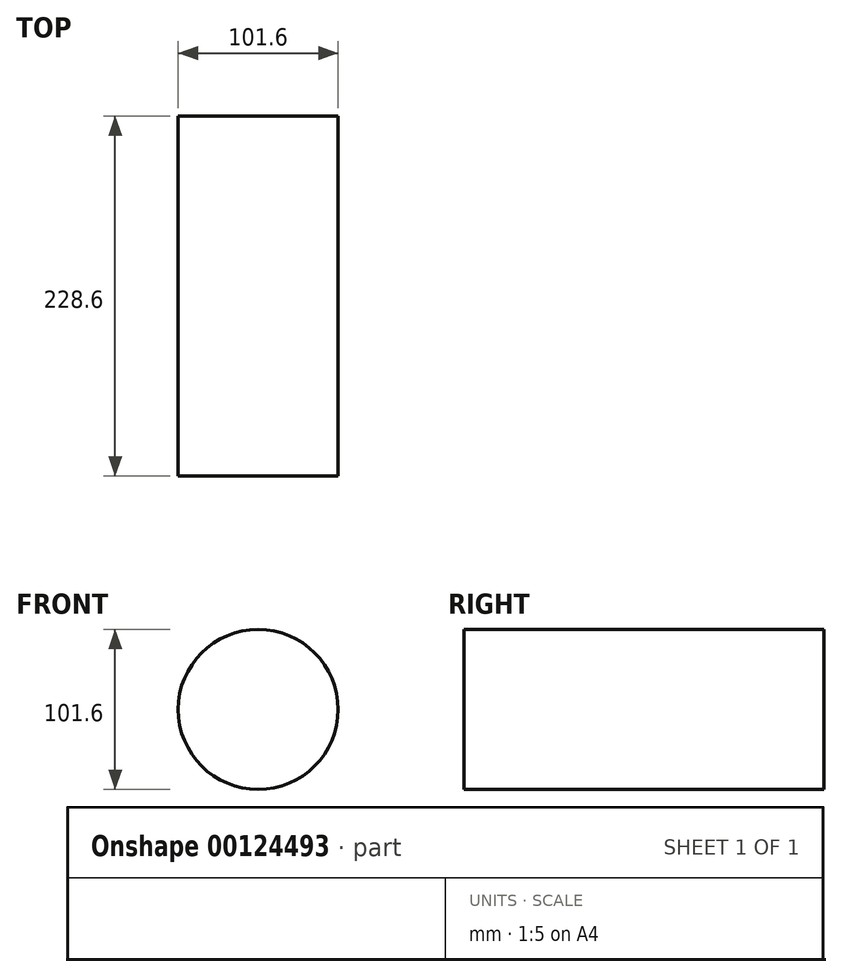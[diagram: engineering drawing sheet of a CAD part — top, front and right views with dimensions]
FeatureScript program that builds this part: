
annotation { "Feature Type Name" : "Feature", "Feature Type Description" : "" }
export const myFeature = defineFeature(function(context is Context, id is Id, definition is map)
    precondition{}
    {
        {
            var Q0;
            Q0=qCreatedBy(makeId("Front.planeOp"),FACE);
            var sketch = newSketch(context, id + "F0", { "sketchPlane" : qUnion([Q0])});
            skCircle(sketch, "E0", {"center": v(0, 0) * mm, "radius": 50.8 * mm});
            skSolve(sketch);
        }
        {
            var Q0;
            Q0=makeQuery(id+"F0.imprint","IMPRINT",FACE,{"disambiguationData":[TD([[makeQuery(id+"F0.imprint","IMPRINT",EDGE,{"derivedFrom":sQuery(id+"F0.wireOp",EDGE,"E0")}),1.0]])]});
            var Q1;
            Q1=sQuery(id+"F0.wireOp",EDGE,"E0");
            extrude(context, id + "F1", {"entities" : qUnion([Q0]), "bodyType" : ToolBodyType.SURFACE, "surfaceEntities" : qUnion([Q1]), "depth" : 228.6 * mm});
        }
    });
